# Revit family: AFX-Cass-Led_Vanity-1
name_source: partatom
category: Lighting Fixtures
units: mm (PartAtom-declared; Revit-internal decimal feet)

## family parameters
Cut with Voids When Loaded = No
Host = Face
Light Source = Yes
Part Type = Normal
Room Calculation Point = No
Round Connector Dimension = Use Diameter
Shared = No

## types (2) — shared parameters
Apparent Load = 0 VA
Assembly Code = D5020200
Canopy Finish = AFX - Aluminum Black
Color Filter = 16777215
Colour Rendering Index = 90CRI
Cord Finish = AFX - Plastic Black
Default Elevation = 48"
Diffuser Finish = AFX - White Acrylic
Dimming Lamp Color Temperature Shift = <None>
Frame Finish = AFX - Aluminum Black
Height = 4"
Keynote = 12500
Manufacturer = AFX Inc
Product Documentation Link = https://www.afxinc.com
Revit File Built By = https://servex-us.com
Tilt Angle = 0.00°
Type Comments = Cass
URL = https://www.afxinc.com
Voltage = 120 V
Wattage Comments = 24W
Width = 5"

## per-type parameters (varying)
| type | Description | Dist Led | Length | Photometric Web File |
| CSSV2404L30D1BK | Contemporary LED vanity with four sided illumination White acrylic diffuser - 5"W x 24"L x 4"H | 12" | 24" | CSSV2404L30D1xx_IES.IES |
| CSSV3604L30D1BK | Contemporary LED vanity with four sided illumination White acrylic diffuser - 5"W x 36"L x 4"H | 10" | 36" | CSSV3604L30D1xx_IES.IES |

note: column(s) folded — value = type name in every type: Model

## geometry (parser evidence)
native form markers: Sweep x2
no freeform markers — native parametric forms only
